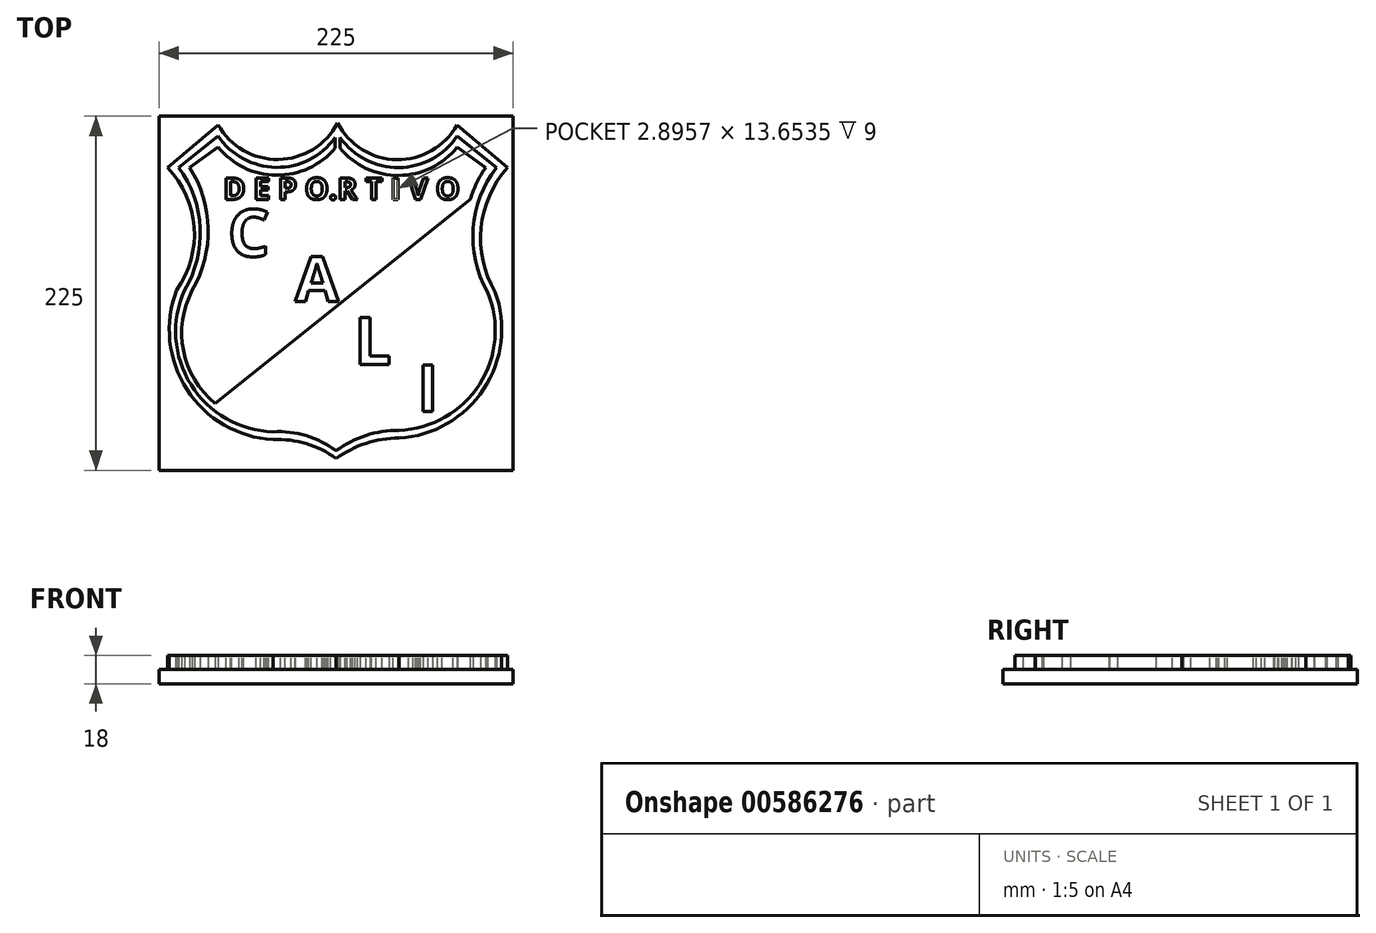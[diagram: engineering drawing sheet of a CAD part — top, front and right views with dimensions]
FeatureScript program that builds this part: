
annotation { "Feature Type Name" : "Feature", "Feature Type Description" : "" }
export const myFeature = defineFeature(function(context is Context, id is Id, definition is map)
    precondition{}
    {
        {
            var Q0;
            Q0=qCreatedBy(makeId("Top.planeOp"),FACE);
            var sketch = newSketch(context, id + "F0", { "sketchPlane" : qUnion([Q0])});
            skPoint(sketch, "E0.middle", {"position": v(0, 0) * mm});
            skLineSegment(sketch, "E1", {"start": v(0.96, 101.2) * mm, "end": v(0, -100) * mm, "construction": true});
            skLineSegment(sketch, "E2", {"start": v(-100, 100) * mm, "end": v(-100, 80) * mm, "construction": true});
            skLineSegment(sketch, "E3", {"start": v(-100, 100) * mm, "end": v(-75, 100) * mm, "construction": true});
            skLineSegment(sketch, "E4", {"start": v(-100, 80) * mm, "end": v(-75, 100) * mm});
            skLineSegment(sketch, "E5", {"start": v(101.96, 99.86) * mm, "end": v(76.96, 99.86) * mm, "construction": true});
            skLineSegment(sketch, "E6", {"start": v(101.96, 99.86) * mm, "end": v(101.96, 79.86) * mm, "construction": true});
            skLineSegment(sketch, "E7", {"start": v(76.96, 99.86) * mm, "end": v(101.96, 79.86) * mm});
            skLineSegment(sketch, "E8", {"start": v(101.96, 79.86) * mm, "end": v(39.46, 79.86) * mm, "construction": true});
            skArc(sketch, "E9", {"start": v(2.46, 98.94) * mm, "mid": v(39.95, 79.86) * mm, "end": v(76.96, 99.86) * mm});
            skLineSegment(sketch, "E10", {"start": v(-100, 80) * mm, "end": v(-100, 40) * mm, "construction": true});
            skLineSegment(sketch, "E11", {"start": v(101.96, 79.86) * mm, "end": v(101.96, 39.86) * mm, "construction": true});
            skLineSegment(sketch, "E12", {"start": v(-101.29, 1.96) * mm, "end": v(-96.29, 1.96) * mm, "construction": true});
            skLineSegment(sketch, "E13", {"start": v(101.09, 0.94) * mm, "end": v(96.09, 0.94) * mm, "construction": true});
            skArc(sketch, "E14", {"start": v(-96.29, 1.96) * mm, "mid": v(-86.3, 41.54) * mm, "end": v(-100, 80) * mm});
            skArc(sketch, "E15", {"start": v(101.96, 79.86) * mm, "mid": v(87.05, 41.3) * mm, "end": v(96.09, 0.94) * mm});
            skLineSegment(sketch, "E16", {"start": v(-101.96, -99.86) * mm, "end": v(-76.96, -99.86) * mm, "construction": true});
            skLineSegment(sketch, "E17", {"start": v(-76.96, -99.86) * mm, "end": v(-76.96, -74.86) * mm, "construction": true});
            skLineSegment(sketch, "E18", {"start": v(-76.96, -74.86) * mm, "end": v(-101.96, -74.86) * mm, "construction": true});
            skLineSegment(sketch, "E19", {"start": v(0, -100) * mm, "end": v(-12, -100) * mm, "construction": true});
            skLineSegment(sketch, "E20", {"start": v(-12, -100) * mm, "end": v(-22, -100) * mm, "construction": true});
            skArc(sketch, "E21", {"start": v(-96.29, 1.96) * mm, "mid": v(-92.21, -58.08) * mm, "end": v(-40, -88) * mm});
            skArc(sketch, "E22", {"start": v(0, -100) * mm, "mid": v(-18.93, -90.45) * mm, "end": v(-40, -88) * mm});
            skLineSegment(sketch, "E23", {"start": v(100, -100) * mm, "end": v(100, -75) * mm, "construction": true});
            skLineSegment(sketch, "E24", {"start": v(75, -75) * mm, "end": v(75, -100) * mm, "construction": true});
            skLineSegment(sketch, "E25", {"start": v(75, -100) * mm, "end": v(100, -100) * mm, "construction": true});
            skLineSegment(sketch, "E26", {"start": v(0, -100) * mm, "end": v(12, -100) * mm, "construction": true});
            skLineSegment(sketch, "E27", {"start": v(0, -100) * mm, "end": v(40, -100) * mm, "construction": true});
            skArc(sketch, "E28", {"start": v(40, -87) * mm, "mid": v(91.2, -57.8) * mm, "end": v(96.09, 0.94) * mm});
            skArc(sketch, "E29", {"start": v(40, -87) * mm, "mid": v(18.96, -90.3) * mm, "end": v(0, -100) * mm});
            skLineSegment(sketch, "E30", {"start": v(-100, 80) * mm, "end": v(-93, 80) * mm, "construction": true});
            skLineSegment(sketch, "E31", {"start": v(-75, 100) * mm, "end": v(-75, 93) * mm, "construction": true});
            skLineSegment(sketch, "E32", {"start": v(0.96, 101.2) * mm, "end": v(0.93, 94.2) * mm, "construction": true});
            skLineSegment(sketch, "E33", {"start": v(-37.5, 80) * mm, "end": v(-37.5, 75) * mm, "construction": true});
            skLineSegment(sketch, "E34", {"start": v(39.46, 79.86) * mm, "end": v(39.46, 74.86) * mm, "construction": true});
            skLineSegment(sketch, "E35", {"start": v(76.96, 99.86) * mm, "end": v(76.96, 92.86) * mm, "construction": true});
            skLineSegment(sketch, "E36", {"start": v(101.96, 79.86) * mm, "end": v(94.96, 79.86) * mm, "construction": true});
            skLineSegment(sketch, "E37", {"start": v(-93, 80) * mm, "end": v(-75, 93) * mm});
            skLineSegment(sketch, "E38", {"start": v(76.96, 92.86) * mm, "end": v(94.96, 79.86) * mm});
            skArc(sketch, "E39", {"start": v(-75, 100) * mm, "mid": v(-38.04, 80) * mm, "end": v(-0.54, 98.96) * mm});
            skArc(sketch, "E40", {"start": v(-75, 93) * mm, "mid": v(-37.93, 75) * mm, "end": v(-0.54, 92.34) * mm});
            skArc(sketch, "E41", {"start": v(2.46, 92.24) * mm, "mid": v(39.85, 74.86) * mm, "end": v(76.96, 92.86) * mm});
            skLineSegment(sketch, "E42", {"start": v(-96.29, 1.96) * mm, "end": v(-91.29, 1.96) * mm, "construction": true});
            skLineSegment(sketch, "E43", {"start": v(-86.25, 40) * mm, "end": v(-81.25, 40) * mm, "construction": true});
            skArc(sketch, "E44", {"start": v(-91.29, 1.96) * mm, "mid": v(-81.27, 41.22) * mm, "end": v(-93, 80) * mm});
            skLineSegment(sketch, "E45", {"start": v(-76.96, -74.86) * mm, "end": v(-76.96, -69.86) * mm, "construction": true});
            skLineSegment(sketch, "E46", {"start": v(-40, -88) * mm, "end": v(-40, -83) * mm, "construction": true});
            skArc(sketch, "E47", {"start": v(-91.29, 1.96) * mm, "mid": v(-96.95, -36.5) * mm, "end": v(-76.96, -69.86) * mm});
            skLineSegment(sketch, "E48", {"start": v(86.96, 39.86) * mm, "end": v(81.96, 39.86) * mm, "construction": true});
            skLineSegment(sketch, "E49", {"start": v(96.09, 0.94) * mm, "end": v(91.09, 0.94) * mm, "construction": true});
            skArc(sketch, "E50", {"start": v(94.96, 79.86) * mm, "mid": v(89.34, 70.09) * mm, "end": v(85.24, 59.59) * mm, "construction": true});
            skLineSegment(sketch, "E51", {"start": v(85.24, 59.59) * mm, "end": v(-76.96, -69.86) * mm});
            skArc(sketch, "E52", {"start": v(94.96, 79.86) * mm, "mid": v(89.34, 70.09) * mm, "end": v(85.24, 59.59) * mm});
            skLineSegment(sketch, "E53", {"start": v(-100, 80) * mm, "end": v(-107, 80) * mm, "construction": true});
            skLineSegment(sketch, "E54", {"start": v(-75, 100) * mm, "end": v(-75, 107) * mm, "construction": true});
            skLineSegment(sketch, "E55", {"start": v(-37.5, 80) * mm, "end": v(-37.5, 85) * mm, "construction": true});
            skLineSegment(sketch, "E56", {"start": v(0.96, 101.2) * mm, "end": v(0.96, 108.2) * mm, "construction": true});
            skLineSegment(sketch, "E57", {"start": v(39.46, 79.86) * mm, "end": v(39.46, 84.86) * mm, "construction": true});
            skLineSegment(sketch, "E58", {"start": v(76.96, 99.86) * mm, "end": v(76.96, 106.86) * mm, "construction": true});
            skLineSegment(sketch, "E59", {"start": v(101.96, 79.86) * mm, "end": v(108.96, 79.86) * mm, "construction": true});
            skLineSegment(sketch, "E60", {"start": v(76.96, 106.86) * mm, "end": v(108.96, 79.86) * mm});
            skArc(sketch, "E61", {"start": v(0.96, 108.2) * mm, "mid": v(38.56, 84.87) * mm, "end": v(76.96, 106.86) * mm});
            skLineSegment(sketch, "E62", {"start": v(-86.25, 40) * mm, "end": v(-93.75, 40) * mm, "construction": true});
            skLineSegment(sketch, "E63", {"start": v(-100, 40) * mm, "end": v(-93.75, 40) * mm, "construction": true});
            skLineSegment(sketch, "E64", {"start": v(-100, 40) * mm, "end": v(-90, 40) * mm, "construction": true});
            skLineSegment(sketch, "E65", {"start": v(-96.29, 1.96) * mm, "end": v(-101.29, 1.96) * mm, "construction": true});
            skArc(sketch, "E66", {"start": v(-101.29, 1.96) * mm, "mid": v(-90.11, 42) * mm, "end": v(-107, 80) * mm});
            skLineSegment(sketch, "E67", {"start": v(-76.96, -74.86) * mm, "end": v(-76.96, -79.86) * mm, "construction": true});
            skLineSegment(sketch, "E68", {"start": v(-40, -88) * mm, "end": v(-40, -93) * mm, "construction": true});
            skArc(sketch, "E69", {"start": v(-101.29, 1.96) * mm, "mid": v(-94.77, -61.09) * mm, "end": v(-40, -93) * mm});
            skLineSegment(sketch, "E70", {"start": v(0, -100) * mm, "end": v(0, -105) * mm, "construction": true});
            skLineSegment(sketch, "E71", {"start": v(-12, -100) * mm, "end": v(-12, -98) * mm, "construction": true});
            skArc(sketch, "E72", {"start": v(0, -105) * mm, "mid": v(-18.93, -95.45) * mm, "end": v(-40, -93) * mm});
            skLineSegment(sketch, "E73", {"start": v(86.96, 39.86) * mm, "end": v(91.96, 39.86) * mm, "construction": true});
            skArc(sketch, "E74", {"start": v(108.96, 79.86) * mm, "mid": v(92.11, 41.69) * mm, "end": v(101.09, 0.94) * mm});
            skLineSegment(sketch, "E75", {"start": v(40, -87) * mm, "end": v(40, -92) * mm, "construction": true});
            skLineSegment(sketch, "E76", {"start": v(75, -75) * mm, "end": v(75, -80) * mm, "construction": true});
            skArc(sketch, "E77", {"start": v(40, -92) * mm, "mid": v(93.82, -60.83) * mm, "end": v(101.09, 0.94) * mm});
            skLineSegment(sketch, "E78", {"start": v(12, -100) * mm, "end": v(12, -98) * mm, "construction": true});
            skArc(sketch, "E79", {"start": v(40, -92) * mm, "mid": v(18.96, -95.3) * mm, "end": v(0, -105) * mm});
            skArc(sketch, "E80", {"start": v(-75, 107) * mm, "mid": v(-36.67, 85) * mm, "end": v(0.96, 108.2) * mm});
            skLineSegment(sketch, "E81", {"start": v(-107, 80) * mm, "end": v(-75, 107) * mm});
            skLineSegment(sketch, "E82", {"start": v(0.96, 108.2) * mm, "end": v(-0.54, 108.2) * mm, "construction": true});
            skLineSegment(sketch, "E83", {"start": v(-0.54, 108.2) * mm, "end": v(2.46, 108.2) * mm, "construction": true});
            skLineSegment(sketch, "E84", {"start": v(-0.54, 105.55) * mm, "end": v(-0.54, 92.34) * mm});
            skLineSegment(sketch, "E85", {"start": v(2.46, 105.53) * mm, "end": v(2.46, 92.24) * mm});
            skLineSegment(sketch, "E86", {"start": v(-0.54, 92.34) * mm, "end": v(0.93, 94.2) * mm, "construction": true});
            skLineSegment(sketch, "E87", {"start": v(2.46, 92.24) * mm, "end": v(0.93, 94.2) * mm, "construction": true});
            skLineSegment(sketch, "E88", {"start": v(-0.54, 98.96) * mm, "end": v(0.96, 101.2) * mm, "construction": true});
            skLineSegment(sketch, "E89", {"start": v(2.46, 98.94) * mm, "end": v(0.96, 101.2) * mm, "construction": true});
            skLineSegment(sketch, "E90.bottom", {"start": v(112.5, 112.5) * mm, "end": v(-112.5, 112.5) * mm});
            skLineSegment(sketch, "E90.top", {"start": v(112.5, -112.5) * mm, "end": v(-112.5, -112.5) * mm});
            skLineSegment(sketch, "E90.left", {"start": v(112.5, 112.5) * mm, "end": v(112.5, -112.5) * mm});
            skLineSegment(sketch, "E90.right", {"start": v(-112.5, 112.5) * mm, "end": v(-112.5, -112.5) * mm});
            skSolve(sketch);
        }
        {
            var Q0;
            Q0=makeQuery(id+"F0.imprint","IMPRINT",FACE,{"disambiguationData":[TD([[makeQuery(id+"F0.imprint","IMPRINT",EDGE,{"derivedFrom":sQuery(id+"F0.wireOp",EDGE,"E4")}),1.0]])]});
            var Q1;
            Q1=makeQuery(id+"F0.imprint","IMPRINT",FACE,{"disambiguationData":[TD([[makeQuery(id+"F0.imprint","IMPRINT",EDGE,{"derivedFrom":sQuery(id+"F0.wireOp",EDGE,"E37")}),-1.0]])]});
            extrude(context, id + "F1", {"entities" : qUnion([Q0, Q1]), "depth" : 9 * mm, "offsetDistance" : 25 * mm});
        }
        {
            var Q0;
            Q0=makeQuery(id+"F1.opExtrude","CAP_FACE",FACE,{"disambiguationData":[OSD([sQuery(id+"F0.wireOp",EDGE,"E4"),sQuery(id+"F0.wireOp",EDGE,"E7"),sQuery(id+"F0.wireOp",EDGE,"E9"),sQuery(id+"F0.wireOp",EDGE,"E14"),sQuery(id+"F0.wireOp",EDGE,"E15"),sQuery(id+"F0.wireOp",EDGE,"E21"),sQuery(id+"F0.wireOp",EDGE,"E22"),sQuery(id+"F0.wireOp",EDGE,"E28"),sQuery(id+"F0.wireOp",EDGE,"E29"),sQuery(id+"F0.wireOp",EDGE,"E37"),sQuery(id+"F0.wireOp",EDGE,"E38"),sQuery(id+"F0.wireOp",EDGE,"E39"),sQuery(id+"F0.wireOp",EDGE,"E40"),sQuery(id+"F0.wireOp",EDGE,"E41"),sQuery(id+"F0.wireOp",EDGE,"E44"),sQuery(id+"F0.wireOp",EDGE,"E47"),sQuery(id+"F0.wireOp",EDGE,"E51"),sQuery(id+"F0.wireOp",EDGE,"E52"),sQuery(id+"F0.wireOp",EDGE,"E60"),sQuery(id+"F0.wireOp",EDGE,"E61"),sQuery(id+"F0.wireOp",EDGE,"E66"),sQuery(id+"F0.wireOp",EDGE,"E69"),sQuery(id+"F0.wireOp",EDGE,"E72"),sQuery(id+"F0.wireOp",EDGE,"E74"),sQuery(id+"F0.wireOp",EDGE,"E77"),sQuery(id+"F0.wireOp",EDGE,"E79"),sQuery(id+"F0.wireOp",EDGE,"E80"),sQuery(id+"F0.wireOp",EDGE,"E81"),sQuery(id+"F0.wireOp",EDGE,"E84"),sQuery(id+"F0.wireOp",EDGE,"E85")])],"isStart":true});
            var sketch = newSketch(context, id + "F2", { "sketchPlane" : qUnion([Q0])});
            skLineSegment(sketch, "E91.bottom", {"start": v(-112.5, -112.5) * mm, "end": v(112.5, -112.5) * mm});
            skLineSegment(sketch, "E91.top", {"start": v(-112.5, 112.5) * mm, "end": v(112.5, 112.5) * mm});
            skLineSegment(sketch, "E91.left", {"start": v(-112.5, -112.5) * mm, "end": v(-112.5, 112.5) * mm});
            skLineSegment(sketch, "E91.right", {"start": v(112.5, -112.5) * mm, "end": v(112.5, 112.5) * mm});
            skPoint(sketch, "E91.middle", {"position": v(0, 0) * mm});
            skSolve(sketch);
        }
        {
            var Q0;
            Q0 = qSketchRegion(id + "F2", true);
            extrude(context, id + "F3", {"entities" : qUnion([Q0]), "operationType" : NewBodyOperationType.ADD, "depth" : 9 * mm, "offsetDistance" : 25 * mm});
        }
        {
            var Q0;
            Q0=makeQuery(id+"F1.opExtrude","CAP_FACE",FACE,{"disambiguationData":[OSD([sQuery(id+"F0.wireOp",EDGE,"E4"),sQuery(id+"F0.wireOp",EDGE,"E7"),sQuery(id+"F0.wireOp",EDGE,"E9"),sQuery(id+"F0.wireOp",EDGE,"E14"),sQuery(id+"F0.wireOp",EDGE,"E15"),sQuery(id+"F0.wireOp",EDGE,"E21"),sQuery(id+"F0.wireOp",EDGE,"E22"),sQuery(id+"F0.wireOp",EDGE,"E28"),sQuery(id+"F0.wireOp",EDGE,"E29"),sQuery(id+"F0.wireOp",EDGE,"E37"),sQuery(id+"F0.wireOp",EDGE,"E38"),sQuery(id+"F0.wireOp",EDGE,"E39"),sQuery(id+"F0.wireOp",EDGE,"E40"),sQuery(id+"F0.wireOp",EDGE,"E41"),sQuery(id+"F0.wireOp",EDGE,"E44"),sQuery(id+"F0.wireOp",EDGE,"E47"),sQuery(id+"F0.wireOp",EDGE,"E51"),sQuery(id+"F0.wireOp",EDGE,"E52"),sQuery(id+"F0.wireOp",EDGE,"E60"),sQuery(id+"F0.wireOp",EDGE,"E61"),sQuery(id+"F0.wireOp",EDGE,"E66"),sQuery(id+"F0.wireOp",EDGE,"E69"),sQuery(id+"F0.wireOp",EDGE,"E72"),sQuery(id+"F0.wireOp",EDGE,"E74"),sQuery(id+"F0.wireOp",EDGE,"E77"),sQuery(id+"F0.wireOp",EDGE,"E79"),sQuery(id+"F0.wireOp",EDGE,"E80"),sQuery(id+"F0.wireOp",EDGE,"E81"),sQuery(id+"F0.wireOp",EDGE,"E84"),sQuery(id+"F0.wireOp",EDGE,"E85")])],"isStart":false});
            var sketch = newSketch(context, id + "F4", { "sketchPlane" : qUnion([Q0])});
            skText(sketch, "E92", { "text": "A", "fontName": "OpenSans-Bold.ttf"});
            skLineSegment(sketch, "E93", {"start": v(-25.86, 23.48) * mm, "end": v(-40.86, 23.48) * mm, "construction": true});
            skText(sketch, "E94", { "text": "C", "fontName": "OpenSans-Bold.ttf"});
            skLineSegment(sketch, "E95", {"start": v(4.14, -5.14) * mm, "end": v(4.14, -15.14) * mm, "construction": true});
            skLineSegment(sketch, "E96", {"start": v(4.14, -15.14) * mm, "end": v(14.14, -15.14) * mm, "construction": true});
            skText(sketch, "E97", { "text": "L", "fontName": "OpenSans-Bold.ttf"});
            skLineSegment(sketch, "E98", {"start": v(38.96, -45.14) * mm, "end": v(53.96, -45.14) * mm, "construction": true});
            skText(sketch, "E99", { "text": "I", "fontName": "OpenSans-Bold.ttf"});
            skLineSegment(sketch, "E100", {"start": v(85.24, 59.59) * mm, "end": v(-83.96, 59.59) * mm, "construction": true});
            skLineSegment(sketch, "E101", {"start": v(97.7, 73.36) * mm, "end": v(-83.96, 73.36) * mm, "construction": true});
            skLineSegment(sketch, "E102", {"start": v(85.24, 59.59) * mm, "end": v(85.24, 73.36) * mm, "construction": true});
            skLineSegment(sketch, "E103", {"start": v(-83.96, 59.59) * mm, "end": v(-83.96, 73.36) * mm, "construction": true});
            skLineSegment(sketch, "E104", {"start": v(0.96, 108.2) * mm, "end": v(0.96, 59.59) * mm, "construction": true});
            skText(sketch, "E105", { "text": "R T I V O", "fontName": "OpenSans-Bold.ttf"});
            skText(sketch, "E106", { "text": "D E P O.", "fontName": "OpenSans-Bold.ttf"});
            const initialGuessF4  = {"E92": [-0.02586, -0.00514, 1, 0, 0.02862], "E94": [-0.06865, 0.02348, 1, 0, 0.03], "E97": [0.01414, -0.04514, 1, 0, 0.03], "E99": [0.05396, -0.07514, 1, 0, 0.03], "E105": [0.00096, 0.05959, 1, 0, 0.01377], "E106": [-0.07165, 0.05959, 1, 0, 0.01377]};
            skSetInitialGuess(sketch, initialGuessF4);
            skSolve(sketch);
        }
        {
            var Q0;
            Q0 = qSketchRegion(id + "F4", true);
            extrude(context, id + "F5", {"entities" : qUnion([Q0]), "operationType" : NewBodyOperationType.REMOVE, "oppositeDirection" : true, "depth" : 9 * mm, "offsetDistance" : 25 * mm});
        }
        {
            var Q0;
            Q0=makeQuery(id+"F3.boolean.opBoolean","SPLIT",FACE,{"disambiguationData":[TD([makeQuery(id+"F1.opExtrude","SWEPT_FACE",FACE,{"disambiguationData":[OSD([sQuery(id+"F0.wireOp",EDGE,"E4")])]})])],"derivedFrom":makeQuery(id+"F3.opExtrude","CAP_FACE",FACE,{"disambiguationData":[OSD([sQuery(id+"F2.wireOp",EDGE,"E91.bottom"),sQuery(id+"F2.wireOp",EDGE,"E91.top"),sQuery(id+"F2.wireOp",EDGE,"E91.left"),sQuery(id+"F2.wireOp",EDGE,"E91.right")])],"isStart":true})});
            var sketch = newSketch(context, id + "F6", { "sketchPlane" : qUnion([Q0])});
            skLineSegment(sketch, "E107", {"start": v(1.56, -5.14) * mm, "end": v(1.56, -15.14) * mm, "construction": true});
            skLineSegment(sketch, "E108", {"start": v(1.56, -15.14) * mm, "end": v(11.56, -15.14) * mm, "construction": true});
            skText(sketch, "E109", { "text": "L", "fontName": "OpenSans-Bold.ttf"});
            skLineSegment(sketch, "E110", {"start": v(36.38, -45.14) * mm, "end": v(51.38, -45.14) * mm, "construction": true});
            skText(sketch, "E111", { "text": "I", "fontName": "OpenSans-Bold.ttf"});
            const initialGuessF6  = {"E109": [0.01156, -0.04514, 1, 0, 0.03], "E111": [0.05138, -0.07514, 1, 0, 0.03]};
            skSetInitialGuess(sketch, initialGuessF6);
            skSolve(sketch);
        }
        {
            var Q0;
            Q0 = qSketchRegion(id + "F6", true);
            extrude(context, id + "F7", {"entities" : qUnion([Q0]), "operationType" : NewBodyOperationType.ADD, "depth" : 9 * mm, "offsetDistance" : 25 * mm});
        }
    });
